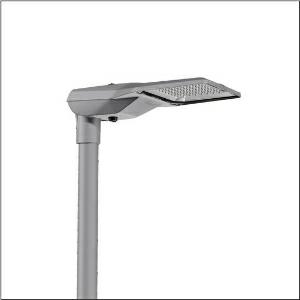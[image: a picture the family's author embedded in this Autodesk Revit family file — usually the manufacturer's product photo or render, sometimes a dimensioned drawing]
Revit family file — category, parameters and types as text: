
# Revit family: streetlight_sl_21_iq_midi___st1_0a_5xe3d51y08nb_3932
name_source: partatom
category: Lighting Fixtures
units: mm (PartAtom-declared; Revit-internal decimal feet)

## family parameters
Cut with Voids When Loaded = No
Host = Face
Light Source = No
Part Type = Normal
Room Calculation Point = No
Round Connector Dimension = Use Diameter
Shared = No

## types (1)
- --- (1 x LED, 18920 lm, 136.6 W, 3000K)
    Apparent Load = 137 VA
    CIE Flux Codes = 40 73 97 100 100
    Color Rendering = 80
    Color Temperature = 3000K
    Default Elevation = 1800 mm
    Description = Streetlight SL 21 iQ midi, mast luminaire, primary light control with lens, of PMMA, primary optical cover: cover, of toughened safety glass, transparent, light distribution: ST1.0a, light emission: direct distribution, primary light characteristic: asymmetric, installation type: post-top, side-entry, LED, High Power LED, rated luminous flux: 18.920lm, luminous efficacy: 139lm/W, light colour: 830, colour temperature: 3000K, control gear: iQ-Street Remote, D4i with power reduction, control: pre-setting: logarithmic dimming characteristic, Street-Remote, Auto-Match, Temp-Guard, Lumen-Switch, Night-Set, Smart-Wire, Light-Fading, Desk-Remote (wireless, voltage-free reading and setting of iQ features in the workshop via application-optimized NFC function/RFID function), optimised constant luminous flux control (CLO 2.0), mains connection: 230..240V, AC, 50/60Hz, start of lifetime: 137W, end of service life: 144W, reduction: 61W, luminaire housing, of diecast aluminium, powder-coated, SITECO metallic grey (DB 702S), corrosivity category C5 high according to DIN EN ISO 12944, please order mast flange separately, inclination adjustable: 0°, 5°, 10°, 15°, sealing non-destructively replaceable, multi-level sealing system, length: 644mm, width: 335mm, height: 110mm, mast flange for spigot size: 42mm (side-entry): 5XC10008XM4, 60/48mm (side-entry/post-top): 5XC10108XM2, 76/60mm (side-entry/post-top): 5XC10108XM1, mounting height: 4..8m, Smart Interface below and above, protection rating (complete): IP66, insulation class (complete): insulation class II (safety insulation), certification: CE, ENEC, ENEC+, VDE, impact resistance: IK10, permissible operating ambient temperature for outdoor applications: -40..+50°C, standard-compliant lighting for roads and squares, packaging unit: 1 piece

Light Distribution: ST1.0a
    Height = 111 mm
    Lamp = 1 x LED
    Lamp Light Flux = 18920 lm
    Lamp Power = 136.6 W
    Lamp count = 1
    Length = 644 mm
    Luminous efficacy = 139 lm/W
    Manufacturer = Siteco
    ModVariant = No
    Model = 5XE3D51Y08NB
    Number of Poles = 1
    OnlyDefault = Yes
    Power Factor = 1
    Product Name = Streetlight SL 21 iQ midi | ST1.0a
    Product group = mast luminaire | pylon top
    ProductGroupID = 6100
    Protection Class = Protection class II
    Protection Degree = IP 66
    RLX_Detail_Level = 1
    RLX_Emergency_Light_Flux = 0 lm
    RLX_Emergency_Type = 0
    RLX_Emergency_Type_DB = No
    RlxData = <blob elided: 91309 chars, md5=888e43d4>
    Socket = socket
    Standby Power = 0 W
    System Light Flux = 18920 lm
    System Power = 137 W
    Type Comments = factory setting: luminous flux: 100 % | dim-lin: 254 | 733 mA
    Type Image = l_1004304.jpg
    URL = http://relux.com
    VarID = @adj_113891
    Voltage = 0 V
    Weight = 0.00 kg
    Width = 336 mm

## geometry (parser evidence)
native form markers: Blend x4, Sweep x12
no freeform markers — native parametric forms only
